# Revit family: IS_Ceraplus_B8653_BIM_DE
name_source: partatom
category: Plumbing Fixtures
revit_build: Autodesk Revit MEP 2015 (Build: 20140606_1530(x64)
units: mm (PartAtom-declared; Revit-internal decimal feet)

## types (1)
- B8653AA - CERAPLUS build-in shower single lever mixer
    Assembly Code = C1030205
    BIMobject category = Showers
    BOSUseNativeGeometries = 1
    Brand url = www.idealstandard.com
    Description = B8653AA CERAPLUS build-in shower single lever mixer
    EAN code = https://4015413323314
    Edition number = 1
    FaucetFunction = mixed
    FaucetOperation = leverhandle
    FaucetType = pillar
    FlushRate = 0 m³
    FlushingRate = 0
    IFC Classification = Valve
    IfcExportAs = Valve
    IfcExportType = BRASSWARE SHOWER
    Installation instructions = http://www.idealspec.co.uk
    Manufacturer name = Ideal Standard
    ManufacturerURL = www.idealstandard.com
    Material = Brass
    Material main = Brass
    Model = B8653AA
    ModelNumber = B8653AA
    NBS Reference Code = 35-06-82
    NBS Reference Description = Shower Mixers
    Name = CERAPLUS build-in shower single lever mixer
    NettWeight = 1,5 kg
    Nominal height = 192
    Nominal width = 158
    NominalDepth = 0 mm  [stored 0 ft]
    NominalHeight = 192 mm  [stored 0.629921 ft]
    NominalLength = 96 mm
    NominalWidth = 157 mm
    OmniClass Code = 23.45.55.17
    OmniClass Description = Mixing Faucets
    Product Guid = ce147c32-4fef-410a-8bfb-a2b9b160a89b
    Product SKU = B8653
    Product data url = https://bimobject.com
    Product family = Ceraplus
    Product group = Shower thermostatic valves
    Product name = CERAPLUS build-in shower single lever mixer
    Product url = www.idealstandard.de/produkte
    ProductInformation = www.idealstandard.de/produkte
    QR code = http://bimobject.com
    Shape = Sculptured
    Size = 192x16x157 mm
    Space = Internal
    SpareParts = www.idealstandard.de/ersatzteile
    Technical description = www.idealstandard.de\produkte
    URL = www.idealstandard.de
    Uniclass 2.0 Code = PR-35-06-82
    Uniclass 2.0 Description = Shower Mixers
    Uniclass 2015 Code = SL_35_80_80
    Uniclass 2015 Name = Showers
    ValveMechanism = ceramic disc
    ValveOperation = lever
    Version = 1
    VolumeUnits = Litres
    WarrantyDurationParts = 5
    WarrantyDurationUnit = year
    Weight Net (Kg) = 1.5
    WorkingPressure = 1-5 Bar

note: [stored X ft] marks values corroborated as IEEE doubles in the binary element streams (Revit-internal decimal feet)

## geometry (parser evidence)
native form markers: Blend x4, Sweep x1
no freeform markers — native parametric forms only
